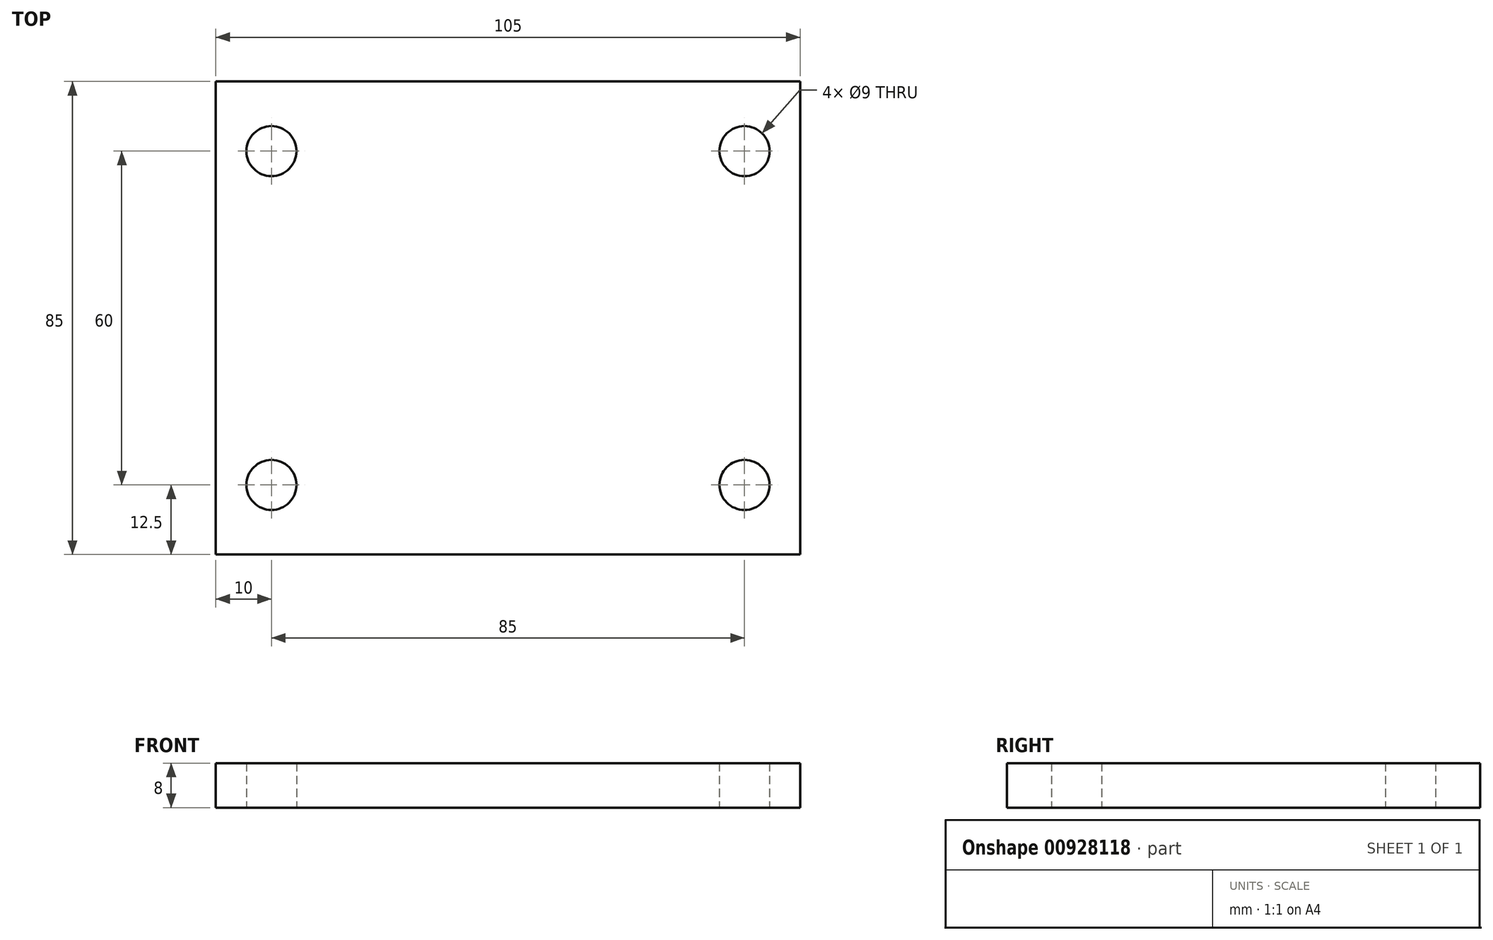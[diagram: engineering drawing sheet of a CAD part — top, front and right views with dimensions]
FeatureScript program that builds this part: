
annotation { "Feature Type Name" : "Feature", "Feature Type Description" : "" }
export const myFeature = defineFeature(function(context is Context, id is Id, definition is map)
    precondition{}
    {
        {
            var Q0;
            Q0=qCreatedBy(makeId("Top.planeOp"),FACE);
            var sketch = newSketch(context, id + "F0", { "sketchPlane" : qUnion([Q0])});
            skLineSegment(sketch, "E0.bottom", {"start": v(52.5, 42.5) * mm, "end": v(-52.5, 42.5) * mm});
            skLineSegment(sketch, "E0.top", {"start": v(52.5, -42.5) * mm, "end": v(-52.5, -42.5) * mm});
            skLineSegment(sketch, "E0.left", {"start": v(52.5, 42.5) * mm, "end": v(52.5, -42.5) * mm});
            skLineSegment(sketch, "E0.right", {"start": v(-52.5, 42.5) * mm, "end": v(-52.5, -42.5) * mm});
            skPoint(sketch, "E0.middle", {"position": v(0, 0) * mm});
            skCircle(sketch, "E1", {"center": v(-42.5, -30) * mm, "radius": 4 * mm});
            skCircle(sketch, "E2", {"center": v(42.5, -30) * mm, "radius": 4 * mm});
            skCircle(sketch, "E3", {"center": v(-42.5, 30) * mm, "radius": 4 * mm});
            skCircle(sketch, "E4", {"center": v(42.5, 30) * mm, "radius": 4 * mm});
            skSolve(sketch);
        }
        {
            var Q0;
            Q0=makeQuery(id+"F0.imprint","IMPRINT",FACE,{"disambiguationData":[TD([[makeQuery(id+"F0.imprint","IMPRINT",EDGE,{"derivedFrom":sQuery(id+"F0.wireOp",EDGE,"E0.bottom")}),1.0]])]});
            var Q1;
            Q1=makeQuery(id+"F0.imprint","IMPRINT",FACE,{"disambiguationData":[TD([[makeQuery(id+"F0.imprint","IMPRINT",EDGE,{"derivedFrom":sQuery(id+"F0.wireOp",EDGE,"E3")}),1.0]])]});
            var Q2;
            Q2=makeQuery(id+"F0.imprint","IMPRINT",FACE,{"disambiguationData":[TD([[makeQuery(id+"F0.imprint","IMPRINT",EDGE,{"derivedFrom":sQuery(id+"F0.wireOp",EDGE,"E4")}),1.0]])]});
            var Q3;
            Q3=makeQuery(id+"F0.imprint","IMPRINT",FACE,{"disambiguationData":[TD([[makeQuery(id+"F0.imprint","IMPRINT",EDGE,{"derivedFrom":sQuery(id+"F0.wireOp",EDGE,"E2")}),1.0]])]});
            var Q4;
            Q4=makeQuery(id+"F0.imprint","IMPRINT",FACE,{"disambiguationData":[TD([[makeQuery(id+"F0.imprint","IMPRINT",EDGE,{"derivedFrom":sQuery(id+"F0.wireOp",EDGE,"E1")}),1.0]])]});
            extrude(context, id + "F1", {"entities" : qUnion([Q0, Q1, Q2, Q3, Q4]), "depth" : 8 * mm, "offsetDistance" : 25 * mm});
        }
        {
            var Q0;
            Q0=sQuery(id+"F0.wireOp",VERTEX,"E3.center");
            var Q1;
            Q1=sQuery(id+"F0.wireOp",VERTEX,"E4.center");
            var Q2;
            Q2=sQuery(id+"F0.wireOp",VERTEX,"E2.center");
            var Q3;
            Q3=sQuery(id+"F0.wireOp",VERTEX,"E1.center");
            var Q4;
            Q4=makeQuery(id+"F1.opExtrude","SWEPT_BODY",BODY,{"disambiguationData":[OSD([sQuery(id+"F0.wireOp",EDGE,"E0.bottom"),sQuery(id+"F0.wireOp",EDGE,"E0.top"),sQuery(id+"F0.wireOp",EDGE,"E0.left"),sQuery(id+"F0.wireOp",EDGE,"E0.right")])]});
            hole(context, id + "F2", {"style" : HoleStyle.SIMPLE, "endStyle" : HoleEndStyle.BLIND, "oppositeDirection" : true, "standardTappedOrClearance" : lookupTablePath({ "fit" : "Normal", "standard" : "ISO", "size" : "M8", "type" : "Clearance" }), "standardBlindInLast" : lookupTablePath({ "fit" : "Normal", "standard" : "ISO", "size" : "M8", "type" : "Clearance" }), "holeDiameter" : 9 * mm, "majorDiameter" : 5 * mm, "holeDepth" : 14 * mm, "isTappedThrough" : true, "tappedDepth" : 12 * mm, "tapClearance" : 3, "locations" : qUnion([Q0, Q1, Q2, Q3]), "scope" : qUnion([Q4])});
        }
    });
